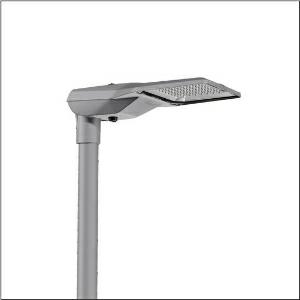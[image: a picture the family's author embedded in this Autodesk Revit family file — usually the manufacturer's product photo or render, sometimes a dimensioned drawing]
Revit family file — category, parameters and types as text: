
# Revit family: streetlight_sl_21_midi___st1_0a_5xe3d33t08lb_3fd1
name_source: partatom
category: Lighting Fixtures
units: mm (PartAtom-declared; Revit-internal decimal feet)

## family parameters
Cut with Voids When Loaded = No
Host = Face
Light Source = No
Part Type = Normal
Room Calculation Point = No
Round Connector Dimension = Use Diameter
Shared = No

## types (1)
- --- (1 x LED, 14340 lm, 99.6 W, 3000K)
    Apparent Load = 100 VA
    CIE Flux Codes = 37 72 97 100 100
    Color Rendering = 70
    Color Temperature = 3000K
    Default Elevation = 1800 mm
    Description = Streetlight SL 21 midi, mast luminaire, primary light control with lens, of PMMA, primary optical cover: cover, of toughened safety glass, transparent, light distribution: ST1.0a, light emission: direct distribution, primary light characteristic: asymmetric, installation type: side-entry, post-top, LED, High Power LED, rated luminous flux: 14.340lm, luminous efficacy: 144lm/W, light colour: 730, colour temperature: 3000K, control gear: D4i, control: flexible luminous flux parameterisation, time-dependent luminous flux control, constant luminous flux control, overheat protection, pre-setting: logarithmic dimming characteristic, mains connection: 230..240V, AC, 50/60Hz, start of lifetime: 100W, end of service life: 102W, reduction: 46W, luminaire housing, of diecast aluminium, powder-coated, SITECO metallic grey (DB 702S), corrosivity category C5 high according to DIN EN ISO 12944, please order mast flange separately, inclination adjustable: 0°, 5°, 10°, 15°, sealing non-destructively replaceable, multi-level sealing system, length: 644mm, width: 335mm, height: 110mm, mast flange for spigot size: 42mm (side-entry): 5XC10008XM4, 60/48mm (side-entry/post-top): 5XC10108XM2, 76/60mm (side-entry/post-top): 5XC10108XM1, mounting height: 4..8m, Smart Interface below and above, protection rating (complete): IP66, insulation class (complete): insulation class II (safety insulation), certification: CE, ENEC, ENEC+, VDE, impact resistance: IK10, permissible operating ambient temperature for outdoor applications: -40..+50°C, standard-compliant lighting for roads and squares, packaging unit: 1 piece

Light Distribution: ST1.0a
    Height = 111 mm
    Lamp = 1 x LED
    Lamp Light Flux = 14340 lm
    Lamp Power = 99.6 W
    Lamp count = 1
    Length = 644 mm
    Luminous efficacy = 144 lm/W
    Manufacturer = Siteco
    ModVariant = No
    Model = 5XE3D33T08LB
    Number of Poles = 1
    OnlyDefault = Yes
    Power Factor = 1
    Product Name = Streetlight SL 21 midi | ST1.0a
    Product group = mast luminaire | pylon top
    ProductGroupID = 6100
    Protection Class = Protection class II
    Protection Degree = IP 66
    RLX_Detail_Level = 1
    RLX_Emergency_Light_Flux = 0 lm
    RLX_Emergency_Type = 0
    RLX_Emergency_Type_DB = No
    RlxData = <blob elided: 26917 chars, md5=8425ed5c>
    Socket = socket
    Standby Power = 0 W
    System Light Flux = 14340 lm
    System Power = 100 W
    Type Comments = factory setting: luminous flux: 100 % | dim-lin: 254 | 1020 mA
    Type Image = l_1004304.jpg
    URL = http://relux.com
    VarID = @adj_031653
    Voltage = 0 V
    Weight = 0.00 kg
    Width = 336 mm

## geometry (parser evidence)
native form markers: Blend x4, Sweep x11
no freeform markers — native parametric forms only
